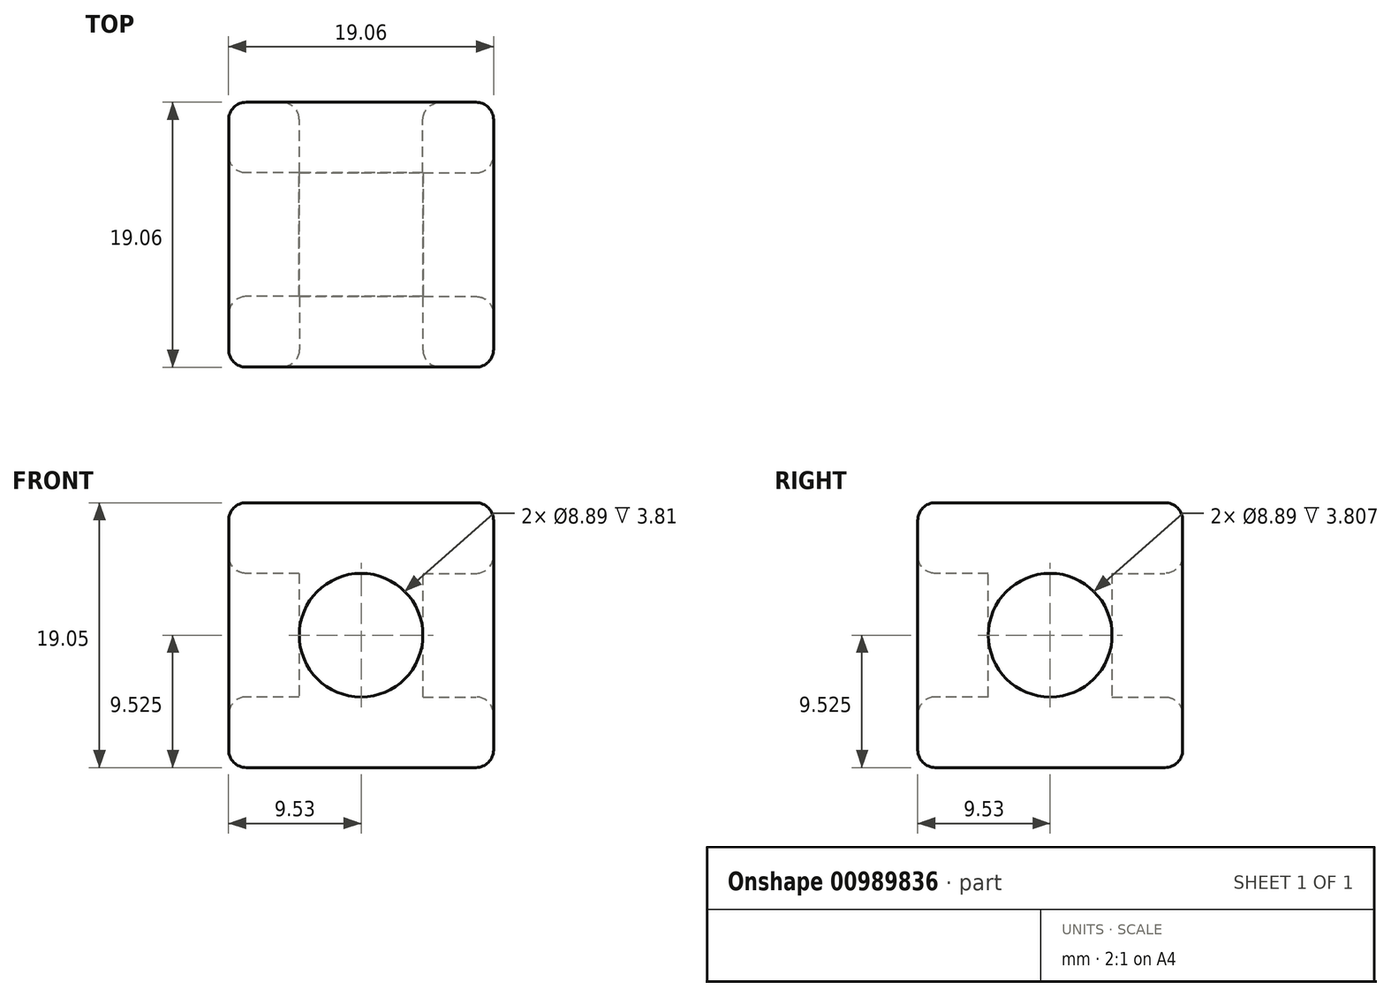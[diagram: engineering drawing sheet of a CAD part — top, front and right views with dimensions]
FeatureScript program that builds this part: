
annotation { "Feature Type Name" : "Feature", "Feature Type Description" : "" }
export const myFeature = defineFeature(function(context is Context, id is Id, definition is map)
    precondition{}
    {
        {
            var Q0;
            Q0=qCreatedBy(makeId("Top.planeOp"),FACE);
            var sketch = newSketch(context, id + "F0", { "sketchPlane" : qUnion([Q0])});
            skLineSegment(sketch, "E0.bottom", {"start": v(-9.53, 9.53) * mm, "end": v(9.53, 9.53) * mm});
            skLineSegment(sketch, "E0.top", {"start": v(-9.53, -9.53) * mm, "end": v(9.53, -9.53) * mm});
            skLineSegment(sketch, "E0.left", {"start": v(-9.53, 9.53) * mm, "end": v(-9.53, -9.53) * mm});
            skLineSegment(sketch, "E0.right", {"start": v(9.53, 9.53) * mm, "end": v(9.53, -9.53) * mm});
            skPoint(sketch, "E0.middle", {"position": v(0, 0) * mm});
            skSolve(sketch);
        }
        {
            var Q0;
            Q0=makeQuery(id+"F0.imprint","IMPRINT",FACE,{"disambiguationData":[TD([[makeQuery(id+"F0.imprint","IMPRINT",EDGE,{"derivedFrom":sQuery(id+"F0.wireOp",EDGE,"E0.bottom")}),-1.0]])]});
            extrude(context, id + "F1", {"entities" : qUnion([Q0]), "depth" : 19.05 * mm, "offsetDistance" : 25.4 * mm});
        }
        {
            var Q0;
            Q0=makeQuery(id+"F1.opExtrude","SWEPT_FACE",FACE,{"disambiguationData":[OSD([sQuery(id+"F0.wireOp",EDGE,"E0.top")])]});
            var sketch = newSketch(context, id + "F2", { "sketchPlane" : qUnion([Q0])});
            skLineSegment(sketch, "E1.0.0", {"start": v(-9.53, 0) * mm, "end": v(9.53, 0) * mm});
            skLineSegment(sketch, "E1.0.1", {"start": v(9.53, 0) * mm, "end": v(9.53, 19.05) * mm});
            skLineSegment(sketch, "E1.0.2", {"start": v(9.53, 19.05) * mm, "end": v(-9.53, 19.05) * mm});
            skLineSegment(sketch, "E1.0.3", {"start": v(-9.53, 19.05) * mm, "end": v(-9.53, 0) * mm});
            skCircle(sketch, "E2", {"center": v(0, 9.53) * mm, "radius": 4.45 * mm});
            skPoint(sketch, "E2.centerSnap0", {"position": v(-9.53, 9.53) * mm});
            skPoint(sketch, "E2.centerSnap1", {"position": v(0, 19.05) * mm});
            skSolve(sketch);
        }
        {
            var Q0;
            Q0=makeQuery(id+"F2.imprint","IMPRINT",FACE,{"disambiguationData":[TD([[makeQuery(id+"F2.imprint","IMPRINT",EDGE,{"derivedFrom":sQuery(id+"F2.wireOp",EDGE,"E2")}),1.0]])]});
            extrude(context, id + "F3", {"entities" : qUnion([Q0]), "operationType" : NewBodyOperationType.REMOVE, "oppositeDirection" : true, "depth" : 5.08 * mm, "offsetDistance" : 25.4 * mm});
        }
        {
            var Q0;
            Q0=makeQuery(id+"F1.opExtrude","SWEPT_FACE",FACE,{"disambiguationData":[OSD([sQuery(id+"F0.wireOp",EDGE,"E0.bottom")])]});
            var sketch = newSketch(context, id + "F4", { "sketchPlane" : qUnion([Q0])});
            skLineSegment(sketch, "E3.0.0", {"start": v(-9.53, 0) * mm, "end": v(9.53, 0) * mm});
            skLineSegment(sketch, "E3.0.1", {"start": v(9.53, 0) * mm, "end": v(9.53, 19.05) * mm});
            skLineSegment(sketch, "E3.0.2", {"start": v(9.53, 19.05) * mm, "end": v(-9.53, 19.05) * mm});
            skLineSegment(sketch, "E3.0.3", {"start": v(-9.53, 19.05) * mm, "end": v(-9.53, 0) * mm});
            skCircle(sketch, "E4", {"center": v(0, 9.53) * mm, "radius": 4.45 * mm});
            skPoint(sketch, "E4.centerSnap0", {"position": v(-9.53, 9.53) * mm});
            skPoint(sketch, "E4.centerSnap1", {"position": v(0, 19.05) * mm});
            skSolve(sketch);
        }
        {
            var Q0;
            Q0=makeQuery(id+"F4.imprint","IMPRINT",FACE,{"disambiguationData":[TD([[makeQuery(id+"F4.imprint","IMPRINT",EDGE,{"derivedFrom":sQuery(id+"F4.wireOp",EDGE,"E4")}),1.0]])]});
            extrude(context, id + "F5", {"entities" : qUnion([Q0]), "operationType" : NewBodyOperationType.REMOVE, "oppositeDirection" : true, "depth" : 5.08 * mm, "offsetDistance" : 25.4 * mm});
        }
        {
            var Q0;
            Q0=makeQuery(id+"F1.opExtrude","SWEPT_FACE",FACE,{"disambiguationData":[OSD([sQuery(id+"F0.wireOp",EDGE,"E0.right")])]});
            var sketch = newSketch(context, id + "F6", { "sketchPlane" : qUnion([Q0])});
            skLineSegment(sketch, "E5.0.0", {"start": v(-9.53, 0) * mm, "end": v(9.53, 0) * mm});
            skLineSegment(sketch, "E5.0.1", {"start": v(9.53, 0) * mm, "end": v(9.53, 19.05) * mm});
            skLineSegment(sketch, "E5.0.2", {"start": v(9.53, 19.05) * mm, "end": v(-9.53, 19.05) * mm});
            skLineSegment(sketch, "E5.0.3", {"start": v(-9.53, 19.05) * mm, "end": v(-9.53, 0) * mm});
            skCircle(sketch, "E6", {"center": v(0, 9.53) * mm, "radius": 4.45 * mm});
            skPoint(sketch, "E6.centerSnap0", {"position": v(-9.53, 9.53) * mm});
            skPoint(sketch, "E6.centerSnap1", {"position": v(0, 19.05) * mm});
            skSolve(sketch);
        }
        {
            var Q0;
            Q0=makeQuery(id+"F6.imprint","IMPRINT",FACE,{"disambiguationData":[TD([[makeQuery(id+"F6.imprint","IMPRINT",EDGE,{"derivedFrom":sQuery(id+"F6.wireOp",EDGE,"E6")}),1.0]])]});
            extrude(context, id + "F7", {"entities" : qUnion([Q0]), "operationType" : NewBodyOperationType.REMOVE, "oppositeDirection" : true, "depth" : 5.08 * mm, "offsetDistance" : 25.4 * mm});
        }
        {
            var Q0;
            Q0=makeQuery(id+"F1.opExtrude","SWEPT_FACE",FACE,{"disambiguationData":[OSD([sQuery(id+"F0.wireOp",EDGE,"E0.left")])]});
            var sketch = newSketch(context, id + "F8", { "sketchPlane" : qUnion([Q0])});
            skCircle(sketch, "E7", {"center": v(0, 9.53) * mm, "radius": 4.45 * mm});
            skPoint(sketch, "E7.centerSnap0", {"position": v(-9.53, 9.53) * mm});
            skPoint(sketch, "E7.centerSnap1", {"position": v(0, 19.05) * mm});
            skSolve(sketch);
        }
        {
            var Q0;
            Q0=makeQuery(id+"F8.imprint","IMPRINT",FACE,{"disambiguationData":[TD([[makeQuery(id+"F8.imprint","IMPRINT",EDGE,{"derivedFrom":sQuery(id+"F8.wireOp",EDGE,"E7")}),1.0]])]});
            extrude(context, id + "F9", {"entities" : qUnion([Q0]), "operationType" : NewBodyOperationType.REMOVE, "oppositeDirection" : true, "depth" : 5.08 * mm, "offsetDistance" : 25.4 * mm});
        }
        {
            var Q0;
            Q0=makeQuery(id+"F1.opExtrude","CAP_FACE",FACE,{"disambiguationData":[OSD([sQuery(id+"F0.wireOp",EDGE,"E0.bottom"),sQuery(id+"F0.wireOp",EDGE,"E0.top"),sQuery(id+"F0.wireOp",EDGE,"E0.left"),sQuery(id+"F0.wireOp",EDGE,"E0.right")])],"isStart":false});
            var Q1;
            Q1=makeQuery(id+"F1.opExtrude","SWEPT_FACE",FACE,{"disambiguationData":[OSD([sQuery(id+"F0.wireOp",EDGE,"E0.left")])]});
            var Q2;
            Q2=makeQuery(id+"F1.opExtrude","SWEPT_FACE",FACE,{"disambiguationData":[OSD([sQuery(id+"F0.wireOp",EDGE,"E0.top")])]});
            var Q3;
            Q3=makeQuery(id+"F1.opExtrude","SWEPT_FACE",FACE,{"disambiguationData":[OSD([sQuery(id+"F0.wireOp",EDGE,"E0.right")])]});
            var Q4;
            Q4=makeQuery(id+"F1.opExtrude","SWEPT_FACE",FACE,{"disambiguationData":[OSD([sQuery(id+"F0.wireOp",EDGE,"E0.bottom")])]});
            var Q5;
            Q5=makeQuery(id+"F1.opExtrude","CAP_FACE",FACE,{"disambiguationData":[OSD([sQuery(id+"F0.wireOp",EDGE,"E0.bottom"),sQuery(id+"F0.wireOp",EDGE,"E0.top"),sQuery(id+"F0.wireOp",EDGE,"E0.left"),sQuery(id+"F0.wireOp",EDGE,"E0.right")])],"isStart":true});
            fillet(context, id + "F10", {"entities" : qUnion([Q0, Q1, Q2, Q3, Q4, Q5]), "radius" : 1.27 * mm, "tangentPropagation" : true, "allowEdgeOverflow" : false});
        }
    });
